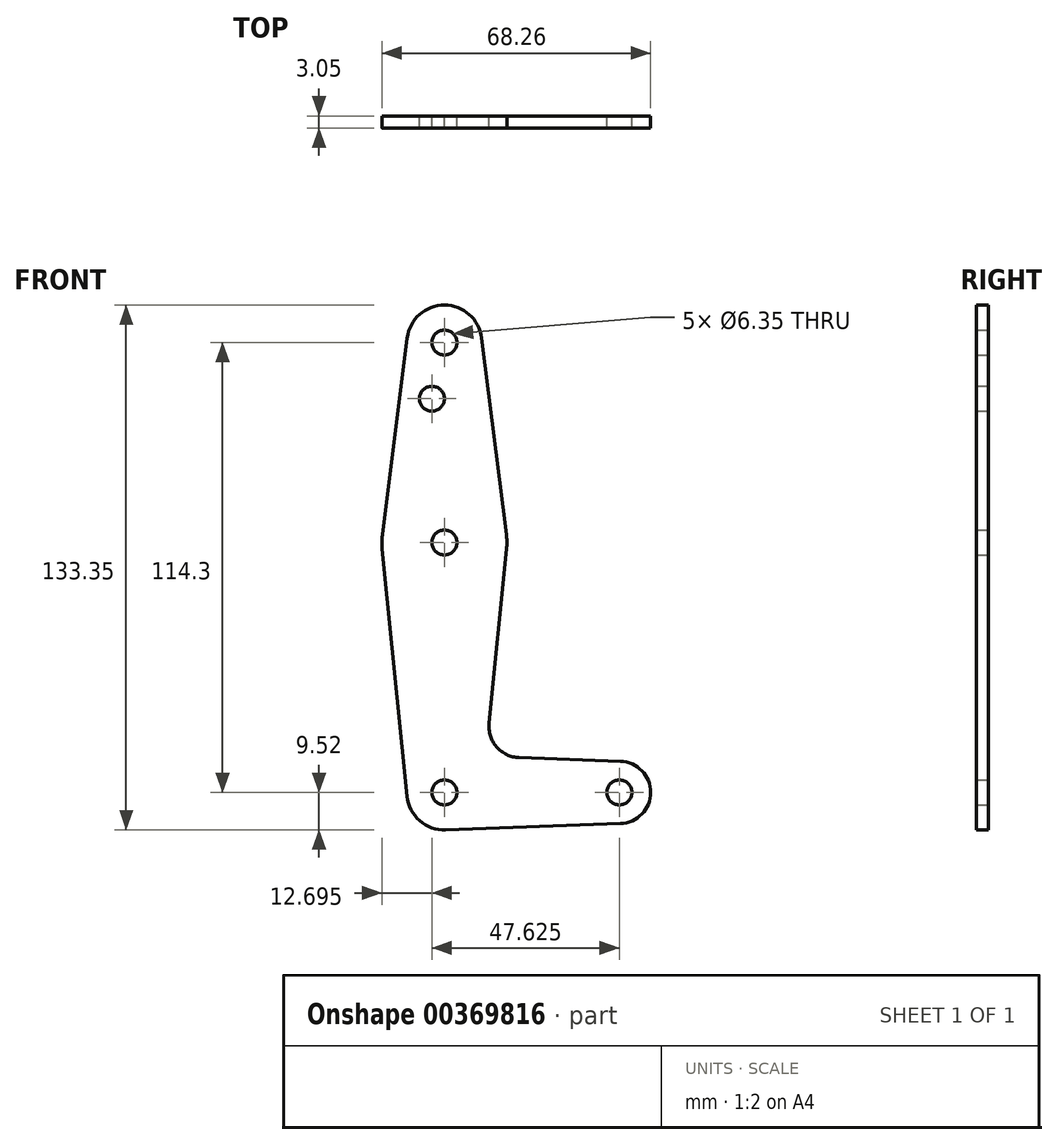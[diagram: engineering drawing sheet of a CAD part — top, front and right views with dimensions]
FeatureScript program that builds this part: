
annotation { "Feature Type Name" : "Feature", "Feature Type Description" : "" }
export const myFeature = defineFeature(function(context is Context, id is Id, definition is map)
    precondition{}
    {
        {
            var Q0;
            Q0=qCreatedBy(makeId("Front.planeOp"),FACE);
            var sketch = newSketch(context, id + "F0", { "sketchPlane" : qUnion([Q0])});
            skLineSegment(sketch, "E0", {"start": v(0, 0) * mm, "end": v(0, 114.3) * mm, "construction": true});
            skLineSegment(sketch, "E1", {"start": v(0, 0) * mm, "end": v(44.45, 0) * mm, "construction": true});
            skCircle(sketch, "E2", {"center": v(0, 0) * mm, "radius": 9.53 * mm});
            skCircle(sketch, "E3", {"center": v(0, 114.3) * mm, "radius": 9.53 * mm});
            skCircle(sketch, "E4", {"center": v(0, 63.5) * mm, "radius": 15.88 * mm});
            skCircle(sketch, "E5", {"center": v(44.45, 0) * mm, "radius": 7.94 * mm});
            skLineSegment(sketch, "E6", {"start": v(-9.45, 115.5) * mm, "end": v(-15.75, 65.48) * mm});
            skLineSegment(sketch, "E7", {"start": v(9.45, 115.5) * mm, "end": v(15.75, 65.48) * mm});
            skLineSegment(sketch, "E8", {"start": v(-15.8, 61.91) * mm, "end": v(-9.48, -0.95) * mm});
            skLineSegment(sketch, "E9", {"start": v(15.8, 61.91) * mm, "end": v(11.34, 17.6) * mm});
            skLineSegment(sketch, "E10", {"start": v(44.73, 7.93) * mm, "end": v(18.97, 8.85) * mm});
            skLineSegment(sketch, "E11", {"start": v(0.34, -9.52) * mm, "end": v(44.73, -7.93) * mm});
            skCircle(sketch, "E12", {"center": v(0, 114.3) * mm, "radius": 3.18 * mm});
            skCircle(sketch, "E13", {"center": v(0, 63.5) * mm, "radius": 3.18 * mm});
            skCircle(sketch, "E14", {"center": v(0, 0) * mm, "radius": 3.18 * mm});
            skCircle(sketch, "E15", {"center": v(44.45, 0) * mm, "radius": 3.18 * mm});
            skCircle(sketch, "E16", {"center": v(-3.18, 100.03) * mm, "radius": 3.18 * mm});
            skLineSegment(sketch, "E17", {"start": v(-3.18, 100.03) * mm, "end": v(0, 100.03) * mm, "construction": true});
            skArc(sketch, "E18.filletArc", {"start": v(11.34, 17.6) * mm, "mid": v(13.26, 11.57) * mm, "end": v(18.97, 8.85) * mm});
            skSolve(sketch);
        }
        {
            var Q0;
            {var subQ1=sQuery(id+"F0.wireOp",EDGE,"E6");Q0=makeQuery(id+"F0.imprint","IMPRINT",FACE,{"disambiguationData":[TD([[makeQuery(id+"F0.imprint","IMPRINT",EDGE,{"derivedFrom":subQ1}),1.0]])]});}
            var Q1;
            {var subQ0=sQuery(id+"F0.wireOp",EDGE,"E8");Q1=makeQuery(id+"F0.imprint","IMPRINT",FACE,{"disambiguationData":[TD([[makeQuery(id+"F0.imprint","IMPRINT",EDGE,{"derivedFrom":subQ0}),1.0]])]});}
            var Q2;
            Q2=makeQuery(id+"F0.imprint","IMPRINT",FACE,{"disambiguationData":[TD([[makeQuery(id+"F0.imprint","IMPRINT",EDGE,{"derivedFrom":sQuery(id+"F0.wireOp",EDGE,"E13")}),-1.0]])]});
            var Q3;
            Q3=makeQuery(id+"F0.imprint","IMPRINT",FACE,{"disambiguationData":[TD([[makeQuery(id+"F0.imprint","IMPRINT",EDGE,{"derivedFrom":sQuery(id+"F0.wireOp",EDGE,"E12")}),-1.0]])]});
            var Q4;
            Q4=makeQuery(id+"F0.imprint","IMPRINT",FACE,{"disambiguationData":[TD([[makeQuery(id+"F0.imprint","IMPRINT",EDGE,{"derivedFrom":sQuery(id+"F0.wireOp",EDGE,"E14")}),-1.0]])]});
            var Q5;
            Q5=makeQuery(id+"F0.imprint","IMPRINT",FACE,{"disambiguationData":[TD([[makeQuery(id+"F0.imprint","IMPRINT",EDGE,{"derivedFrom":sQuery(id+"F0.wireOp",EDGE,"E15")}),-1.0]])]});
            extrude(context, id + "F1", {"entities" : qUnion([Q0, Q1, Q2, Q3, Q4, Q5]), "depth" : 3.05 * mm});
        }
    });
